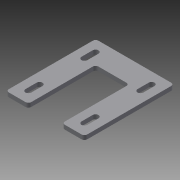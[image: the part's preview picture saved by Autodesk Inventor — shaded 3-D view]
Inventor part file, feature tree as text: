
AUTODESK INVENTOR PART (.ipt)
format: ipt  version: 2013 (Build 170138000, 138)  size: 118,272 bytes
history: native  units: in
note: dims shown in document units (in); Inventor stores cm internally (conversion verified against a paired STEP export)
features: extrude x1, fillet x1, mirror x1, sketch x1
ambient origin geometry x8: Origin, YZ Plane, XZ Plane, XY Plane, X Axis, Y Axis, Z Axis, Center Point
bodies: Solid1 (feature_tree)
feature tree (4):
  extrude  "Extrusion1"  Depth=0.1875in TaperAngle=0.0deg
  fillet  "Fillet1"  Radius=1.75in
  mirror  "Mirror2"
  sketch  "Sketch1"  dims[d1=4.0in d6=0.1875in d7=0.0in d8=1.75in d9=1.0in d11=0.26in d12=0.37in d13=0.37in d14=0.5in d15=0.5in d16=0.26in d17=0.5in d18=0.5in d19=1.0in d20=0.125in]
